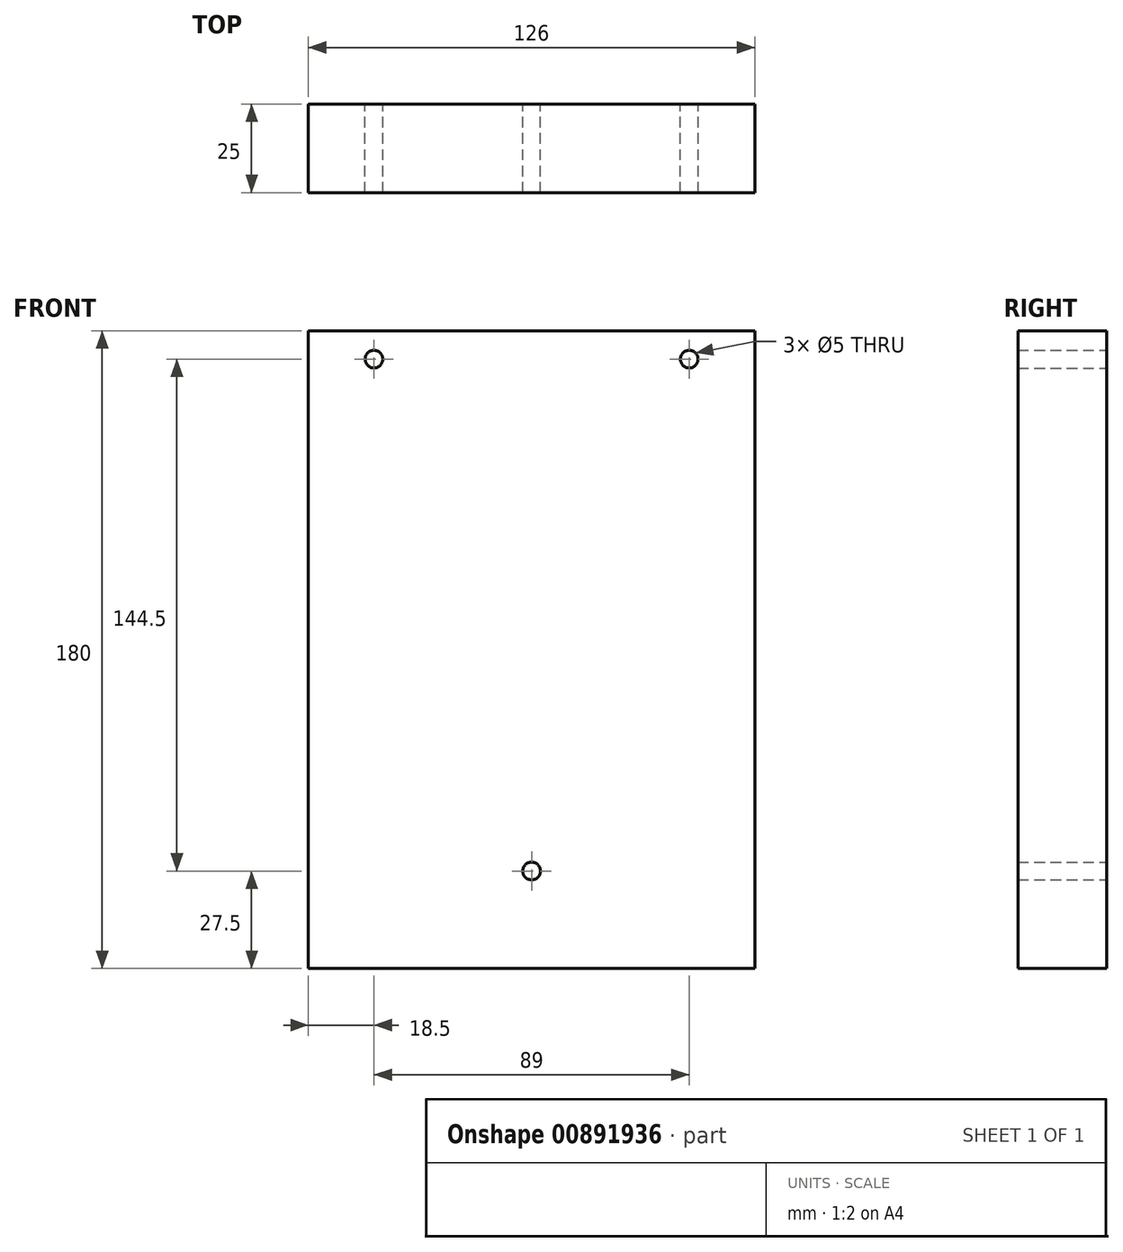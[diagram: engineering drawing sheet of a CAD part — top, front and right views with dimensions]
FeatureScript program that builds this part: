
annotation { "Feature Type Name" : "Feature", "Feature Type Description" : "" }
export const myFeature = defineFeature(function(context is Context, id is Id, definition is map)
    precondition{}
    {
        {
            var Q0;
            Q0=qCreatedBy(makeId("Front.planeOp"),FACE);
            var sketch = newSketch(context, id + "F0", { "sketchPlane" : qUnion([Q0])});
            skLineSegment(sketch, "E0.bottom", {"start": v(63, 90) * mm, "end": v(-63, 90) * mm});
            skLineSegment(sketch, "E0.top", {"start": v(63, -90) * mm, "end": v(-63, -90) * mm});
            skLineSegment(sketch, "E0.left", {"start": v(63, 90) * mm, "end": v(63, -90) * mm});
            skLineSegment(sketch, "E0.right", {"start": v(-63, 90) * mm, "end": v(-63, -90) * mm});
            skPoint(sketch, "E0.middle", {"position": v(0, 0) * mm});
            skCircle(sketch, "E1", {"center": v(0, -62.5) * mm, "radius": 2.5 * mm});
            skCircle(sketch, "E2", {"center": v(-44.5, 82) * mm, "radius": 2.5 * mm});
            skLineSegment(sketch, "E3", {"start": v(-104.89, 82) * mm, "end": v(119.54, 82) * mm, "construction": true});
            skCircle(sketch, "E4.MirrorC", {"center": v(44.5, 82) * mm, "radius": 2.5 * mm});
            skLineSegment(sketch, "E5.MirrorCS", {"start": v(104.89, 82) * mm, "end": v(-119.54, 82) * mm, "construction": true});
            skLineSegment(sketch, "E6.MirrorCS", {"start": v(-63, 90) * mm, "end": v(63, 90) * mm});
            skSolve(sketch);
        }
        {
            var Q0;
            Q0 = qSketchRegion(id + "F0", true);
            extrude(context, id + "F1", {"entities" : qUnion([Q0]), "depth" : 25 * mm, "offsetDistance" : 25 * mm});
        }
    });
